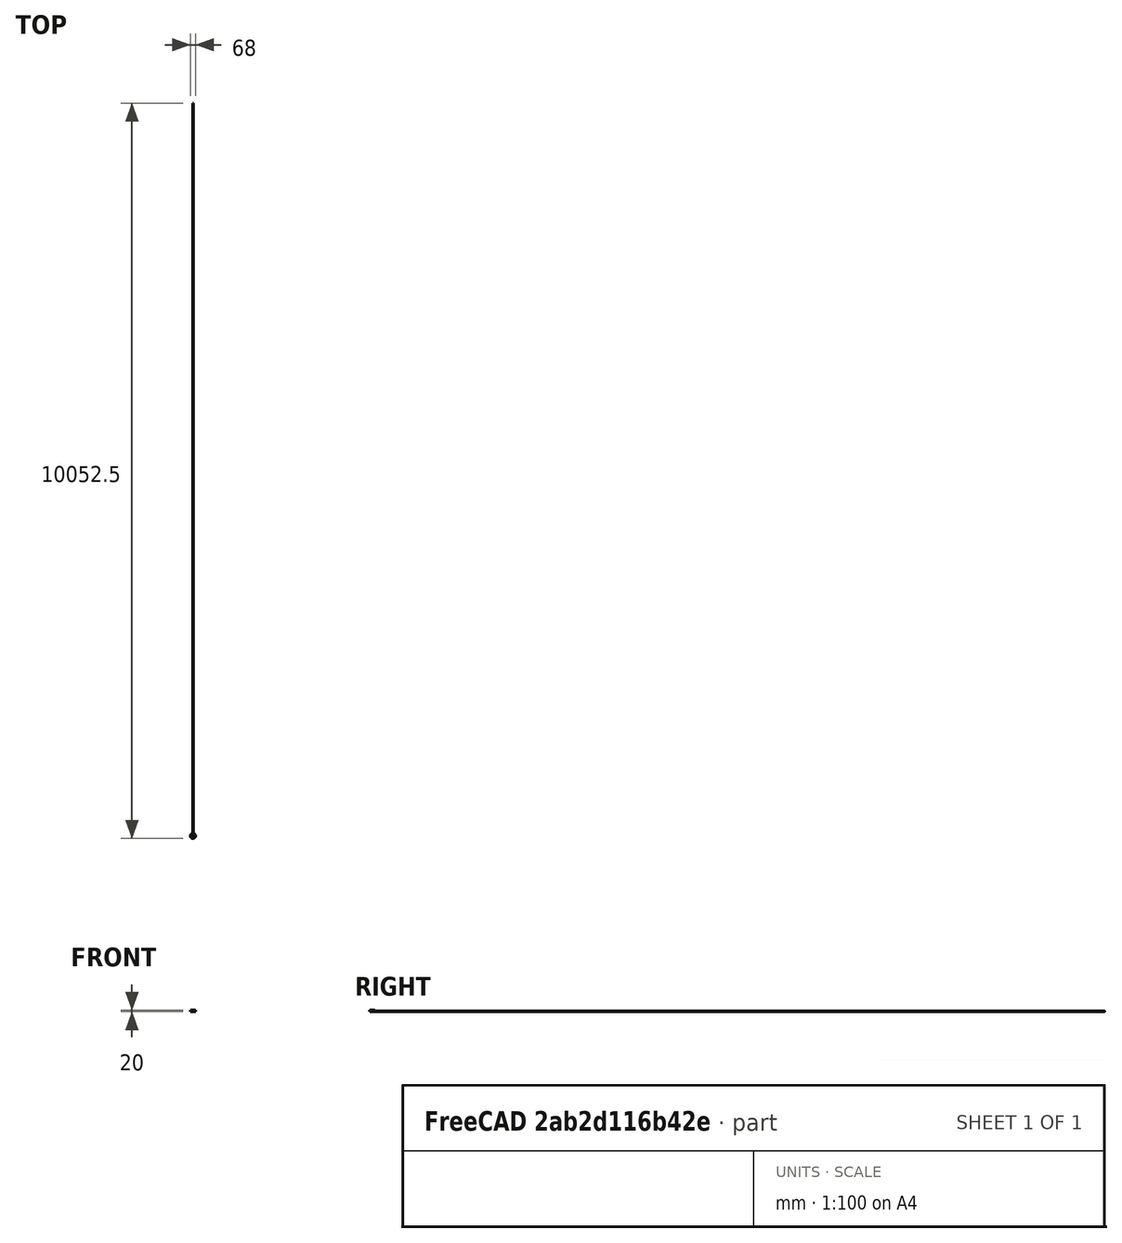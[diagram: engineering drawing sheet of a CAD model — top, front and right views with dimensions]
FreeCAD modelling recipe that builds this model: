
FCSTD DOCUMENT  (FreeCAD 0.16R)
Label: bathtest
License: All rights reserved
LicenseURL: http://en.wikipedia.org/wiki/All_rights_reserved
objects: Sketcher::SketchObject×4, PartDesign::Pocket×3, PartDesign::Pad×1, Mesh::Feature×1
note: 12 computed .brp shape members not serialized (recipe doc carries the construction recipe); baked Part::Feature solids carry a one-line shape summary decoded from their .brp

FEATURE [Sketcher::SketchObject] Sketch
  sketch-geometry (1):
    g0: Circle CenterX=0 CenterY=0 CenterZ=0 NormalX=0 NormalY=0 NormalZ=1 Radius=34
  constraints (2):
    c: Coincident(g0,g-1)
    c: Radius(g0) = 34
FEATURE [PartDesign::Pad] Pad
  Length = 20
  Length2 = 100
  Sketch = -> Sketch
  Type = 0
FEATURE [Sketcher::SketchObject] Sketch001
  Placement = pos=(0,0,20) rot=(0,0,1;0rad)
  Support = -> Pad [Face3]
  sketch-geometry (1):
    g0: Circle CenterX=0 CenterY=0 CenterZ=0 NormalX=0 NormalY=0 NormalZ=1 Radius=22.4
  constraints (2):
    c: Coincident(g0,g-1)
    c: Radius(g0) = 22.4
FEATURE [PartDesign::Pocket] Pocket
  Length = 8
  Sketch = -> Sketch001
  Type = 0
FEATURE [Sketcher::SketchObject] Sketch002
  Placement = pos=(0,0,12) rot=(0,0,1;0rad)
  Support = -> Pocket [Face5]
  sketch-geometry (4):
    g0: LineSegment StartX=-8.6 StartY=18.5 StartZ=0 EndX=8.6 EndY=18.5 EndZ=0
    g1: LineSegment StartX=8.6 StartY=18.5 StartZ=0 EndX=8.6 EndY=-18.5 EndZ=0
    g2: LineSegment StartX=8.6 StartY=-18.5 StartZ=0 EndX=-8.6 EndY=-18.5 EndZ=0
    g3: LineSegment StartX=-8.6 StartY=-18.5 StartZ=0 EndX=-8.6 EndY=18.5 EndZ=0
  constraints (12):
    c: Coincident(g0,g1)
    c: Coincident(g1,g2)
    c: Coincident(g2,g3)
    c: Coincident(g3,g0)
    c: Horizontal(g0)
    c: Horizontal(g2)
    c: Vertical(g1)
    c: Vertical(g3)
    c: Distance(g0) = 17.2
    c: Symmetric(g0,g0,g-2)
    c: DistanceY(g0) = 18.5
    c: Symmetric(g1,g0,g-1)
FEATURE [PartDesign::Pocket] Pocket001
  Length = 10.5
  Sketch = -> Sketch002
  Type = 0
FEATURE [Sketcher::SketchObject] Sketch003
  ExternalGeometry = -> [Pocket001]
  Placement = pos=(0,18.5,0) rot=(1,0,0;1.5708rad)
  Support = -> Pocket001 [Face7]
  sketch-geometry (1):
    g0: Circle CenterX=0 CenterY=6.5 CenterZ=0 NormalX=0 NormalY=0 NormalZ=1 Radius=2
  constraints (3):
    c: Radius(g0) = 2
    c: PointOnObject(g0,g-2)
    c: Distance(g0,g-3) = 5
FEATURE [PartDesign::Pocket] Pocket002
  Length = 5
  Sketch = -> Sketch003
  Type = 1
FEATURE [Mesh::Feature] Mesh  label="Pocket002 (Meshed)"
